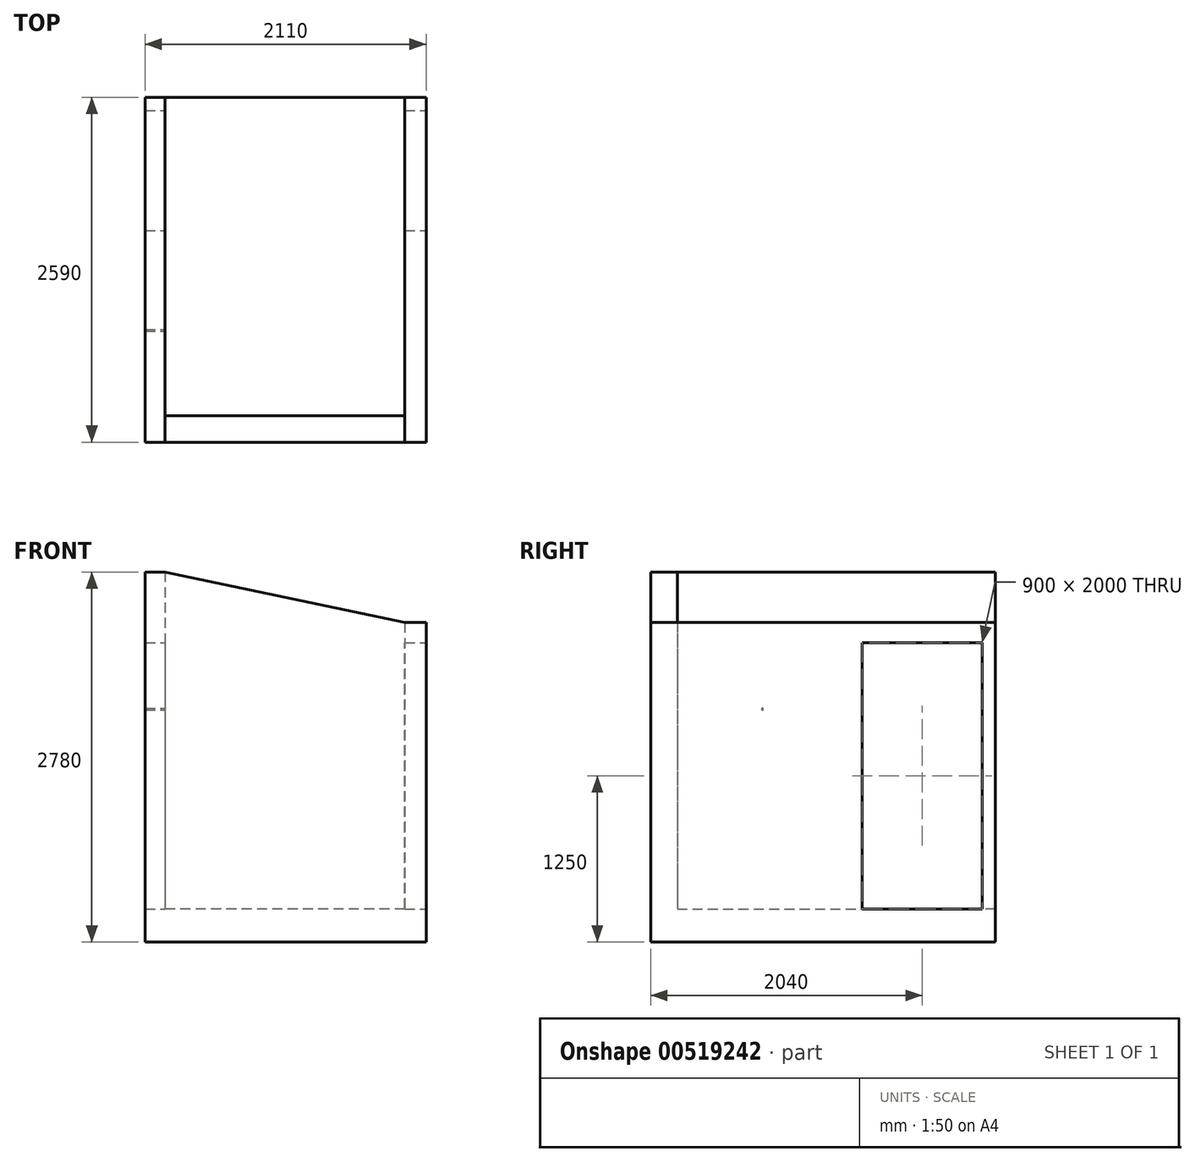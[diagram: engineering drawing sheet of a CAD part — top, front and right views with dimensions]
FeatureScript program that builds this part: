
annotation { "Feature Type Name" : "Feature", "Feature Type Description" : "" }
export const myFeature = defineFeature(function(context is Context, id is Id, definition is map)
    precondition{}
    {
        {
            var Q0;
            Q0=qCreatedBy(makeId("Top.planeOp"),FACE);
            var sketch = newSketch(context, id + "F0", { "sketchPlane" : qUnion([Q0])});
            skLineSegment(sketch, "E0.bottom", {"start": v(0, 0) * mm, "end": v(10600, 0) * mm});
            skLineSegment(sketch, "E0.top", {"start": v(0, -6350) * mm, "end": v(9400, -6350) * mm});
            skLineSegment(sketch, "E0.left", {"start": v(0, 0) * mm, "end": v(0, -6350) * mm});
            skLineSegment(sketch, "E0.right", {"start": v(10600, 0) * mm, "end": v(10600, -5300) * mm});
            skLineSegment(sketch, "E1.top", {"start": v(10600, -5300) * mm, "end": v(9400, -5300) * mm});
            skLineSegment(sketch, "E1.right", {"start": v(9400, -6350) * mm, "end": v(9400, -5300) * mm});
            skLineSegment(sketch, "E2.top", {"start": v(3900, -5150) * mm, "end": v(6300, -5150) * mm});
            skLineSegment(sketch, "E2.left", {"start": v(3900, -6150) * mm, "end": v(3900, -5150) * mm});
            skLineSegment(sketch, "E2.right", {"start": v(6300, -6150) * mm, "end": v(6300, -5150) * mm});
            skLineSegment(sketch, "E3.top", {"start": v(3900, -6150) * mm, "end": v(6300, -6150) * mm});
            skSolve(sketch);
        }
        {
            var Q0;
            Q0=qSketchRegion(id+"F0",true);
            extrude(context, id + "F1", {"entities" : qUnion([Q0]), "depth" : 250 * mm});
        }
        {
            var Q0;
            Q0=makeQuery(id+"F1.opExtrude","CAP_FACE",FACE,{"disambiguationData":[OSD([sQuery(id+"F0.wireOp",EDGE,"E0.bottom"),sQuery(id+"F0.wireOp",EDGE,"E0.top"),sQuery(id+"F0.wireOp",EDGE,"E0.left"),sQuery(id+"F0.wireOp",EDGE,"E0.right")])],"isStart":false});
            var sketch = newSketch(context, id + "F2", { "sketchPlane" : qUnion([Q0])});
            skLineSegment(sketch, "E4.bottom", {"start": v(200, -200) * mm, "end": v(3750, -200) * mm});
            skLineSegment(sketch, "E4.top", {"start": v(200, -6150) * mm, "end": v(3750, -6150) * mm});
            skLineSegment(sketch, "E4.left", {"start": v(200, -200) * mm, "end": v(200, -6150) * mm});
            skLineSegment(sketch, "E4.right", {"start": v(10400, -300) * mm, "end": v(10400, -3610) * mm});
            skLineSegment(sketch, "E5.bottom", {"start": v(9240, -6150) * mm, "end": v(7440, -6150) * mm});
            skLineSegment(sketch, "E5.top", {"start": v(10400, -3610) * mm, "end": v(7440, -3610) * mm});
            skLineSegment(sketch, "E6.top", {"start": v(3750, -5050) * mm, "end": v(3900, -5050) * mm});
            skLineSegment(sketch, "E6.left", {"start": v(3750, -6150) * mm, "end": v(3750, -5050) * mm});
            skLineSegment(sketch, "E6.right", {"start": v(3900, -6150) * mm, "end": v(3900, -5050) * mm});
            skLineSegment(sketch, "E7.top", {"start": v(3750, -300) * mm, "end": v(3900, -300) * mm});
            skLineSegment(sketch, "E7.left", {"start": v(3750, -200) * mm, "end": v(3750, -300) * mm});
            skLineSegment(sketch, "E7.right", {"start": v(3900, -280) * mm, "end": v(3900, -300) * mm});
            skLineSegment(sketch, "E8.top", {"start": v(4800, -1180) * mm, "end": v(4950, -1180) * mm});
            skLineSegment(sketch, "E8.left", {"start": v(4800, -280) * mm, "end": v(4800, -1180) * mm});
            skLineSegment(sketch, "E8.right", {"start": v(4950, -400) * mm, "end": v(4950, -1180) * mm});
            skLineSegment(sketch, "E9.top", {"start": v(7290, -300) * mm, "end": v(7440, -300) * mm});
            skLineSegment(sketch, "E9.left", {"start": v(7290, -200) * mm, "end": v(7290, -300) * mm});
            skLineSegment(sketch, "E10.top", {"start": v(9240, -3760) * mm, "end": v(7440, -3760) * mm});
            skLineSegment(sketch, "E10.right", {"start": v(7440, -6150) * mm, "end": v(7440, -3760) * mm});
            skLineSegment(sketch, "E11.top", {"start": v(7290, -2960) * mm, "end": v(7440, -2960) * mm});
            skLineSegment(sketch, "E11.left", {"start": v(7290, -6150) * mm, "end": v(7290, -2960) * mm});
            skLineSegment(sketch, "E11.right", {"start": v(7440, -3610) * mm, "end": v(7440, -2960) * mm});
            skLineSegment(sketch, "E12.bottom", {"start": v(0, 0) * mm, "end": v(10600, 0) * mm});
            skLineSegment(sketch, "E12.top", {"start": v(0, -6350) * mm, "end": v(9400, -6350) * mm});
            skLineSegment(sketch, "E12.left", {"start": v(0, 0) * mm, "end": v(0, -6350) * mm});
            skLineSegment(sketch, "E12.right", {"start": v(10600, 0) * mm, "end": v(10600, -3760) * mm});
            skLineSegment(sketch, "E13.trimOffspring", {"start": v(5250, -200) * mm, "end": v(7290, -200) * mm});
            skLineSegment(sketch, "E14.trimOffspring", {"start": v(3900, -6150) * mm, "end": v(7290, -6150) * mm});
            skLineSegment(sketch, "E15.top", {"start": v(4950, -400) * mm, "end": v(5250, -400) * mm});
            skLineSegment(sketch, "E15.right", {"start": v(5250, -200) * mm, "end": v(5250, -400) * mm});
            skLineSegment(sketch, "E16.top", {"start": v(3900, -280) * mm, "end": v(4800, -280) * mm});
            skLineSegment(sketch, "E17.trimOffspring", {"start": v(7440, -6150) * mm, "end": v(9240, -6150) * mm});
            skLineSegment(sketch, "E18.trimOffspring", {"start": v(9240, -3760) * mm, "end": v(9240, -6150) * mm});
            skLineSegment(sketch, "E19", {"start": v(10600, -3760) * mm, "end": v(9400, -3760) * mm});
            skLineSegment(sketch, "E20", {"start": v(9400, -3760) * mm, "end": v(9400, -6350) * mm});
            skLineSegment(sketch, "E21", {"start": v(7440, -300) * mm, "end": v(10400, -300) * mm});
            skSolve(sketch);
        }
        {
            var Q0;
            Q0=qSketchRegion(id+"F2",true);
            extrude(context, id + "F3", {"entities" : qUnion([Q0]), "operationType" : NewBodyOperationType.ADD, "depth" : 2320 * mm});
        }
        {
            var Q0;
            Q0=makeQuery(id+"F3.boolean.opBoolean","MERGE",FACE,{"derivedFrom":[makeQuery(id+"F1.opExtrude","SWEPT_FACE",FACE,{"disambiguationData":[OSD([sQuery(id+"F0.wireOp",EDGE,"E1.right")])]}),makeQuery(id+"F3.opExtrude","SWEPT_FACE",FACE,{"disambiguationData":[OSD([sQuery(id+"F2.wireOp",EDGE,"E20")])]})]});
            var sketch = newSketch(context, id + "F4", { "sketchPlane" : qUnion([Q0])});
            skLineSegment(sketch, "E22.bottom", {"start": v(-4760, 250) * mm, "end": v(-3860, 250) * mm});
            skLineSegment(sketch, "E22.top", {"start": v(-4760, 2250) * mm, "end": v(-3860, 2250) * mm});
            skLineSegment(sketch, "E22.left", {"start": v(-4760, 250) * mm, "end": v(-4760, 2250) * mm});
            skLineSegment(sketch, "E22.right", {"start": v(-3860, 250) * mm, "end": v(-3860, 2250) * mm});
            skSolve(sketch);
        }
        {
            var Q0;
            Q0=qSketchRegion(id+"F4",true);
            extrude(context, id + "F5", {"entities" : qUnion([Q0]), "operationType" : NewBodyOperationType.REMOVE, "endBound" : BoundingType.THROUGH_ALL, "oppositeDirection" : true, "depth" : 3000 * mm});
        }
        {
            var Q0;
            Q0=makeQuery(id+"F3.boolean.opBoolean","MERGE",FACE,{"derivedFrom":[makeQuery(id+"F1.opExtrude","SWEPT_FACE",FACE,{"disambiguationData":[OSD([sQuery(id+"F0.wireOp",EDGE,"E0.top")])]}),makeQuery(id+"F3.opExtrude","SWEPT_FACE",FACE,{"disambiguationData":[OSD([sQuery(id+"F2.wireOp",EDGE,"E12.top")])]})]});
            var sketch = newSketch(context, id + "F6", { "sketchPlane" : qUnion([Q0])});
            skLineSegment(sketch, "E23.bottom", {"start": v(7240, 2200) * mm, "end": v(6240, 2200) * mm});
            skLineSegment(sketch, "E23.top", {"start": v(7240, 800) * mm, "end": v(6240, 800) * mm});
            skLineSegment(sketch, "E23.left", {"start": v(7240, 2200) * mm, "end": v(7240, 800) * mm});
            skLineSegment(sketch, "E23.right", {"start": v(6240, 2200) * mm, "end": v(6240, 800) * mm});
            skLineSegment(sketch, "E24.bottom", {"start": v(2600, 2200) * mm, "end": v(3600, 2200) * mm});
            skLineSegment(sketch, "E24.top", {"start": v(2600, 800) * mm, "end": v(3600, 800) * mm});
            skLineSegment(sketch, "E24.left", {"start": v(2600, 2200) * mm, "end": v(2600, 800) * mm});
            skLineSegment(sketch, "E24.right", {"start": v(3600, 2200) * mm, "end": v(3600, 800) * mm});
            skLineSegment(sketch, "E25.bottom", {"start": v(9450, 2200) * mm, "end": v(10350, 2200) * mm});
            skLineSegment(sketch, "E25.top", {"start": v(9450, 1800) * mm, "end": v(10350, 1800) * mm});
            skLineSegment(sketch, "E25.left", {"start": v(9450, 2200) * mm, "end": v(9450, 1800) * mm});
            skLineSegment(sketch, "E25.right", {"start": v(10350, 2200) * mm, "end": v(10350, 1800) * mm});
            skSolve(sketch);
        }
        {
            var Q0;
            Q0=qSketchRegion(id+"F6",true);
            var Q1;
            Q1=makeQuery(id+"F3.opExtrude","SWEPT_FACE",FACE,{"disambiguationData":[OSD([sQuery(id+"F2.wireOp",EDGE,"E9.top"),sQuery(id+"F2.wireOp",EDGE,"E21")])]});
            extrude(context, id + "F7", {"entities" : qUnion([Q0]), "operationType" : NewBodyOperationType.REMOVE, "endBound" : BoundingType.UP_TO_SURFACE, "oppositeDirection" : true, "endBoundEntityFace" : qUnion([Q1]), "depth" : 25 * mm});
        }
        {
            var Q0;
            Q0=makeQuery(id+"F3.opExtrude","SWEPT_FACE",FACE,{"disambiguationData":[OSD([sQuery(id+"F2.wireOp",EDGE,"E4.right")])]});
            var sketch = newSketch(context, id + "F8", { "sketchPlane" : qUnion([Q0])});
            skLineSegment(sketch, "E26.bottom", {"start": v(680, 2100) * mm, "end": v(1600, 2100) * mm});
            skLineSegment(sketch, "E26.top", {"start": v(680, 1180) * mm, "end": v(1600, 1180) * mm});
            skLineSegment(sketch, "E26.left", {"start": v(680, 2100) * mm, "end": v(680, 1180) * mm});
            skLineSegment(sketch, "E26.right", {"start": v(1600, 2100) * mm, "end": v(1600, 1180) * mm});
            skLineSegment(sketch, "E27.bottom", {"start": v(1860, 2100) * mm, "end": v(2860, 2100) * mm});
            skLineSegment(sketch, "E27.top", {"start": v(1860, 1180) * mm, "end": v(2860, 1180) * mm});
            skLineSegment(sketch, "E27.left", {"start": v(1860, 2100) * mm, "end": v(1860, 1180) * mm});
            skLineSegment(sketch, "E27.right", {"start": v(2860, 2100) * mm, "end": v(2860, 1180) * mm});
            skSolve(sketch);
        }
        {
            var Q0;
            Q0=qSketchRegion(id+"F8",true);
            extrude(context, id + "F9", {"entities" : qUnion([Q0]), "operationType" : NewBodyOperationType.REMOVE, "endBound" : BoundingType.UP_TO_NEXT, "oppositeDirection" : true, "depth" : 25 * mm});
        }
        {
            var Q0;
            Q0=makeQuery(id+"F3.opExtrude","SWEPT_FACE",FACE,{"disambiguationData":[OSD([sQuery(id+"F2.wireOp",EDGE,"E4.left")])]});
            var sketch = newSketch(context, id + "F10", { "sketchPlane" : qUnion([Q0])});
            skLineSegment(sketch, "E28.bottom", {"start": v(-3660, 2250) * mm, "end": v(-2660, 2250) * mm});
            skLineSegment(sketch, "E28.top", {"start": v(-3660, 750) * mm, "end": v(-2660, 750) * mm});
            skLineSegment(sketch, "E28.left", {"start": v(-3660, 2250) * mm, "end": v(-3660, 750) * mm});
            skLineSegment(sketch, "E28.right", {"start": v(-2660, 2250) * mm, "end": v(-2660, 750) * mm});
            skLineSegment(sketch, "E29.bottom", {"start": v(-2560, 2250) * mm, "end": v(-1560, 2250) * mm});
            skLineSegment(sketch, "E29.top", {"start": v(-2560, 750) * mm, "end": v(-1560, 750) * mm});
            skLineSegment(sketch, "E29.left", {"start": v(-2560, 2250) * mm, "end": v(-2560, 750) * mm});
            skLineSegment(sketch, "E29.right", {"start": v(-1560, 2250) * mm, "end": v(-1560, 750) * mm});
            skLineSegment(sketch, "E30.bottom", {"start": v(-1460, 2250) * mm, "end": v(-460, 2250) * mm});
            skLineSegment(sketch, "E30.top", {"start": v(-1460, 750) * mm, "end": v(-460, 750) * mm});
            skLineSegment(sketch, "E30.left", {"start": v(-1460, 2250) * mm, "end": v(-1460, 750) * mm});
            skLineSegment(sketch, "E30.right", {"start": v(-460, 2250) * mm, "end": v(-460, 750) * mm});
            skSolve(sketch);
        }
        {
            var Q0;
            Q0=qSketchRegion(id+"F10",true);
            extrude(context, id + "F11", {"entities" : qUnion([Q0]), "operationType" : NewBodyOperationType.REMOVE, "endBound" : BoundingType.UP_TO_NEXT, "oppositeDirection" : true, "depth" : 25 * mm});
        }
        {
            var Q0;
            Q0=makeQuery(id+"F3.opExtrude","CAP_FACE",FACE,{"disambiguationData":[OSD([sQuery(id+"F2.wireOp",EDGE,"E4.bottom"),sQuery(id+"F2.wireOp",EDGE,"E4.top"),sQuery(id+"F2.wireOp",EDGE,"E4.left"),sQuery(id+"F2.wireOp",EDGE,"E4.right"),sQuery(id+"F2.wireOp",EDGE,"E5.top"),sQuery(id+"F2.wireOp",EDGE,"E6.top"),sQuery(id+"F2.wireOp",EDGE,"E6.left"),sQuery(id+"F2.wireOp",EDGE,"E6.right"),sQuery(id+"F2.wireOp",EDGE,"E7.top"),sQuery(id+"F2.wireOp",EDGE,"E7.left"),sQuery(id+"F2.wireOp",EDGE,"E7.right"),sQuery(id+"F2.wireOp",EDGE,"E8.top"),sQuery(id+"F2.wireOp",EDGE,"E8.left"),sQuery(id+"F2.wireOp",EDGE,"E8.right"),sQuery(id+"F2.wireOp",EDGE,"E9.top"),sQuery(id+"F2.wireOp",EDGE,"E9.left"),sQuery(id+"F2.wireOp",EDGE,"E9.right"),sQuery(id+"F2.wireOp",EDGE,"E10.top"),sQuery(id+"F2.wireOp",EDGE,"E10.right"),sQuery(id+"F2.wireOp",EDGE,"E11.top"),sQuery(id+"F2.wireOp",EDGE,"E11.left"),sQuery(id+"F2.wireOp",EDGE,"E11.right"),sQuery(id+"F2.wireOp",EDGE,"E12.bottom"),sQuery(id+"F2.wireOp",EDGE,"E12.top"),sQuery(id+"F2.wireOp",EDGE,"E12.left"),sQuery(id+"F2.wireOp",EDGE,"E12.right"),sQuery(id+"F2.wireOp",EDGE,"E13.trimOffspring"),sQuery(id+"F2.wireOp",EDGE,"f96be5dc-ae23-419c-a534-e8c19ccc8482.trimOffspring"),sQuery(id+"F2.wireOp",EDGE,"E14.trimOffspring"),sQuery(id+"F2.wireOp",EDGE,"E15.top"),sQuery(id+"F2.wireOp",EDGE,"E15.right"),sQuery(id+"F2.wireOp",EDGE,"E16.top"),sQuery(id+"F2.wireOp",EDGE,"E17.trimOffspring"),sQuery(id+"F2.wireOp",EDGE,"E18.trimOffspring"),sQuery(id+"F2.wireOp",EDGE,"E19"),sQuery(id+"F2.wireOp",EDGE,"E20")])],"isStart":false});
            var sketch = newSketch(context, id + "F12", { "sketchPlane" : qUnion([Q0])});
            skLineSegment(sketch, "E31.bottom", {"start": v(7290, -300) * mm, "end": v(7440, -300) * mm});
            skLineSegment(sketch, "E31.top", {"start": v(7290, -2960) * mm, "end": v(7440, -2960) * mm});
            skLineSegment(sketch, "E31.left", {"start": v(7290, -300) * mm, "end": v(7290, -2960) * mm});
            skLineSegment(sketch, "E31.right", {"start": v(7440, -300) * mm, "end": v(7440, -2960) * mm});
            skSolve(sketch);
        }
        {
            var Q0;
            Q0=qSketchRegion(id+"F12",true);
            extrude(context, id + "F13", {"entities" : qUnion([Q0]), "operationType" : NewBodyOperationType.ADD, "oppositeDirection" : true, "depth" : 280 * mm});
        }
        {
            var Q0;
            Q0=makeQuery(id+"F3.boolean.opBoolean","MERGE",FACE,{"derivedFrom":[makeQuery(id+"F1.opExtrude","SWEPT_FACE",FACE,{"disambiguationData":[OSD([sQuery(id+"F0.wireOp",EDGE,"E3.top")])]}),makeQuery(id+"F3.opExtrude","SWEPT_FACE",FACE,{"disambiguationData":[OSD([sQuery(id+"F2.wireOp",EDGE,"E14.trimOffspring")])]})]});
            var sketch = newSketch(context, id + "F14", { "sketchPlane" : qUnion([Q0])});
            skLineSegment(sketch, "E32", {"start": v(-6350, 250) * mm, "end": v(-6350, 540) * mm});
            skLineSegment(sketch, "E33", {"start": v(-6350, 540) * mm, "end": v(-6045, 540) * mm});
            skLineSegment(sketch, "E34", {"start": v(-6045, 540) * mm, "end": v(-6045, 830) * mm});
            skLineSegment(sketch, "E35", {"start": v(-6045, 830) * mm, "end": v(-5740, 830) * mm});
            skLineSegment(sketch, "E36", {"start": v(-5740, 830) * mm, "end": v(-5740, 1120) * mm});
            skLineSegment(sketch, "E37", {"start": v(-5740, 1120) * mm, "end": v(-5435, 1120) * mm});
            skLineSegment(sketch, "E38", {"start": v(-5435, 1120) * mm, "end": v(-5435, 1410) * mm});
            skLineSegment(sketch, "E39", {"start": v(-5435, 1410) * mm, "end": v(-5130, 1410) * mm});
            skLineSegment(sketch, "E40", {"start": v(-5130, 1410) * mm, "end": v(-5130, 1700) * mm});
            skLineSegment(sketch, "E41", {"start": v(-5130, 1700) * mm, "end": v(-4825, 1700) * mm});
            skLineSegment(sketch, "E42", {"start": v(-4825, 1700) * mm, "end": v(-4825, 1990) * mm});
            skLineSegment(sketch, "E43", {"start": v(-4825, 1990) * mm, "end": v(-4520, 1990) * mm});
            skLineSegment(sketch, "E44", {"start": v(-4520, 1990) * mm, "end": v(-4520, 2280) * mm});
            skLineSegment(sketch, "E45", {"start": v(-4520, 2280) * mm, "end": v(-4215, 2280) * mm});
            skLineSegment(sketch, "E46", {"start": v(-4215, 2280) * mm, "end": v(-4215, 2570) * mm});
            skLineSegment(sketch, "E47", {"start": v(-4215, 2570) * mm, "end": v(-3900, 2570) * mm});
            skLineSegment(sketch, "E48.0", {"start": v(-4165, 2520) * mm, "end": v(-3900, 2520) * mm});
            skLineSegment(sketch, "E48.1", {"start": v(-4165, 2230) * mm, "end": v(-4165, 2520) * mm});
            skLineSegment(sketch, "E48.2", {"start": v(-4470, 2230) * mm, "end": v(-4165, 2230) * mm});
            skLineSegment(sketch, "E48.3", {"start": v(-4470, 1940) * mm, "end": v(-4470, 2230) * mm});
            skLineSegment(sketch, "E48.4", {"start": v(-4775, 1940) * mm, "end": v(-4470, 1940) * mm});
            skLineSegment(sketch, "E48.5", {"start": v(-4775, 1650) * mm, "end": v(-4775, 1940) * mm});
            skLineSegment(sketch, "E48.6", {"start": v(-5995, 780) * mm, "end": v(-5690, 780) * mm});
            skLineSegment(sketch, "E48.7", {"start": v(-5995, 490) * mm, "end": v(-5995, 780) * mm});
            skLineSegment(sketch, "E48.8", {"start": v(-6300, 490) * mm, "end": v(-5995, 490) * mm});
            skLineSegment(sketch, "E48.9", {"start": v(-6300, 250) * mm, "end": v(-6300, 490) * mm});
            skLineSegment(sketch, "E48.10", {"start": v(-5690, 780) * mm, "end": v(-5690, 1070) * mm});
            skLineSegment(sketch, "E48.11", {"start": v(-5690, 1070) * mm, "end": v(-5385, 1070) * mm});
            skLineSegment(sketch, "E48.12", {"start": v(-5385, 1070) * mm, "end": v(-5385, 1360) * mm});
            skLineSegment(sketch, "E48.13", {"start": v(-5385, 1360) * mm, "end": v(-5080, 1360) * mm});
            skLineSegment(sketch, "E48.14", {"start": v(-5080, 1360) * mm, "end": v(-5080, 1650) * mm});
            skLineSegment(sketch, "E48.15", {"start": v(-5080, 1650) * mm, "end": v(-4775, 1650) * mm});
            skLineSegment(sketch, "E49", {"start": v(-3900, 2570) * mm, "end": v(-3900, 2520) * mm});
            skLineSegment(sketch, "E50", {"start": v(-6350, 250) * mm, "end": v(-6300, 250) * mm});
            skLineSegment(sketch, "E51", {"start": v(-3900, 2570) * mm, "end": v(-3900, 250) * mm, "construction": true});
            skSolve(sketch);
        }
        {
            var Q0;
            Q0=qSketchRegion(id+"F14",true);
            extrude(context, id + "F15", {"entities" : qUnion([Q0]), "operationType" : NewBodyOperationType.ADD, "depth" : 950 * mm});
        }
        {
            var Q0;
            Q0=makeQuery(id+"F15.opExtrude","CAP_FACE",FACE,{"disambiguationData":[OSD([sQuery(id+"F14.wireOp",EDGE,"E32"),sQuery(id+"F14.wireOp",EDGE,"E33"),sQuery(id+"F14.wireOp",EDGE,"E34"),sQuery(id+"F14.wireOp",EDGE,"E35"),sQuery(id+"F14.wireOp",EDGE,"E36"),sQuery(id+"F14.wireOp",EDGE,"E37"),sQuery(id+"F14.wireOp",EDGE,"E38"),sQuery(id+"F14.wireOp",EDGE,"E39"),sQuery(id+"F14.wireOp",EDGE,"E40"),sQuery(id+"F14.wireOp",EDGE,"E41"),sQuery(id+"F14.wireOp",EDGE,"E42"),sQuery(id+"F14.wireOp",EDGE,"E43"),sQuery(id+"F14.wireOp",EDGE,"E44"),sQuery(id+"F14.wireOp",EDGE,"E45"),sQuery(id+"F14.wireOp",EDGE,"E46"),sQuery(id+"F14.wireOp",EDGE,"E47"),sQuery(id+"F14.wireOp",EDGE,"E48.0"),sQuery(id+"F14.wireOp",EDGE,"E48.1"),sQuery(id+"F14.wireOp",EDGE,"E48.2"),sQuery(id+"F14.wireOp",EDGE,"E48.3"),sQuery(id+"F14.wireOp",EDGE,"E48.4"),sQuery(id+"F14.wireOp",EDGE,"E48.5"),sQuery(id+"F14.wireOp",EDGE,"E48.6"),sQuery(id+"F14.wireOp",EDGE,"E48.7"),sQuery(id+"F14.wireOp",EDGE,"E48.8"),sQuery(id+"F14.wireOp",EDGE,"E48.9"),sQuery(id+"F14.wireOp",EDGE,"E48.10"),sQuery(id+"F14.wireOp",EDGE,"E48.11"),sQuery(id+"F14.wireOp",EDGE,"E48.12"),sQuery(id+"F14.wireOp",EDGE,"E48.13"),sQuery(id+"F14.wireOp",EDGE,"E48.14"),sQuery(id+"F14.wireOp",EDGE,"E48.15"),sQuery(id+"F14.wireOp",EDGE,"E49"),sQuery(id+"F14.wireOp",EDGE,"E50")])],"isStart":false});
            var sketch = newSketch(context, id + "F16", { "sketchPlane" : qUnion([Q0])});
            skLineSegment(sketch, "E52", {"start": v(-6350, 540) * mm, "end": v(-4215, 2570) * mm});
            skLineSegment(sketch, "E53", {"start": v(-3900, 2570) * mm, "end": v(-3900, 2475.76) * mm});
            skLineSegment(sketch, "E54", {"start": v(-6300, 250) * mm, "end": v(-4165, 2230) * mm});
            skLineSegment(sketch, "E55", {"start": v(-4165, 2230) * mm, "end": v(-3900, 2475.76) * mm});
            skLineSegment(sketch, "E56", {"start": v(-6350, 540) * mm, "end": v(-6350, 250) * mm});
            skLineSegment(sketch, "E57", {"start": v(-6350, 250) * mm, "end": v(-6300, 250) * mm});
            skLineSegment(sketch, "E58", {"start": v(-4215, 2570) * mm, "end": v(-3900, 2570) * mm});
            skSolve(sketch);
        }
        {
            var Q0;
            Q0=qSketchRegion(id+"F16",true);
            extrude(context, id + "F17", {"entities" : qUnion([Q0]), "operationType" : NewBodyOperationType.ADD, "depth" : 50 * mm});
        }
        {
            var Q0;
            {var subQ0=sQuery(id+"F0.wireOp",EDGE,"E3.top");var subQ1=sQuery(id+"F0.wireOp",EDGE,"E2.right");var subQ2=sQuery(id+"F0.wireOp",EDGE,"E2.left");var subQ3=sQuery(id+"F0.wireOp",EDGE,"E2.top");var subQ4=sQuery(id+"F0.wireOp",EDGE,"E1.right");var subQ5=sQuery(id+"F0.wireOp",EDGE,"E1.top");var subQ6=sQuery(id+"F0.wireOp",EDGE,"E0.right");var subQ7=makeQuery(id+"F1.opExtrude","CAP_FACE",FACE,{"disambiguationData":[OSD([sQuery(id+"F0.wireOp",EDGE,"E0.bottom"),sQuery(id+"F0.wireOp",EDGE,"E0.top"),sQuery(id+"F0.wireOp",EDGE,"E0.left"),subQ6,subQ5,subQ4,subQ3,subQ2,subQ1,subQ0])],"isStart":false});Q0=makeQuery(id+"F5.boolean.opBoolean","MERGE",FACE,{"derivedFrom":[makeQuery(id+"F3.boolean.opBoolean","SPLIT",FACE,{"disambiguationData":[TD([makeQuery(id+"F1.opExtrude","SWEPT_FACE",FACE,{"disambiguationData":[OSD([subQ6])]})])],"derivedFrom":subQ7}),makeQuery(id+"F3.boolean.opBoolean","SPLIT",FACE,{"disambiguationData":[TD([makeQuery(id+"F1.opExtrude","SWEPT_FACE",FACE,{"disambiguationData":[OSD([subQ3])]})])],"derivedFrom":subQ7}),makeQuery(id+"F3.boolean.opBoolean","SPLIT",FACE,{"disambiguationData":[TD([makeQuery(id+"F3.opExtrude","SWEPT_FACE",FACE,{"disambiguationData":[OSD([sQuery(id+"F2.wireOp",EDGE,"E10.top")])]})])],"derivedFrom":subQ7}),makeQuery(id+"F5.opExtrude","SWEPT_FACE",FACE,{"disambiguationData":[OSD([sQuery(id+"F4.wireOp",EDGE,"E22.bottom")])]})]});}
            var sketch = newSketch(context, id + "F18", { "sketchPlane" : qUnion([Q0])});
            skLineSegment(sketch, "E59.bottom", {"start": v(6045, -5150) * mm, "end": v(6005, -5150) * mm});
            skLineSegment(sketch, "E59.top", {"start": v(6045, -5100) * mm, "end": v(6005, -5100) * mm});
            skLineSegment(sketch, "E59.left", {"start": v(6050, -5145) * mm, "end": v(6050, -5105) * mm});
            skLineSegment(sketch, "E59.right", {"start": v(6000, -5145) * mm, "end": v(6000, -5105) * mm});
            skPoint(sketch, "E60.visualSharp", {"position": v(6000, -5100) * mm});
            skArc(sketch, "E60.filletArc", {"start": v(6005, -5100) * mm, "mid": v(6001.46, -5101.46) * mm, "end": v(6000, -5105) * mm});
            skPoint(sketch, "E61.visualSharp", {"position": v(6050, -5100) * mm});
            skArc(sketch, "E61.filletArc", {"start": v(6050, -5105) * mm, "mid": v(6048.54, -5101.46) * mm, "end": v(6045, -5100) * mm});
            skPoint(sketch, "E62.visualSharp", {"position": v(6050, -5150) * mm});
            skArc(sketch, "E62.filletArc", {"start": v(6045, -5150) * mm, "mid": v(6048.54, -5148.54) * mm, "end": v(6050, -5145) * mm});
            skPoint(sketch, "E63.visualSharp", {"position": v(6000, -5150) * mm});
            skArc(sketch, "E63.filletArc", {"start": v(6000, -5145) * mm, "mid": v(6001.46, -5148.54) * mm, "end": v(6005, -5150) * mm});
            skPoint(sketch, "E64.1.0.0", {"position": v(5700, -5150) * mm});
            skLineSegment(sketch, "E64.1.0.1", {"start": v(5745, -5150) * mm, "end": v(5705, -5150) * mm});
            skLineSegment(sketch, "E64.1.0.2", {"start": v(5745, -5100) * mm, "end": v(5705, -5100) * mm});
            skPoint(sketch, "E64.1.0.3", {"position": v(5700, -5100) * mm});
            skLineSegment(sketch, "E64.1.0.4", {"start": v(5750, -5145) * mm, "end": v(5750, -5105) * mm});
            skPoint(sketch, "E64.1.0.5", {"position": v(5750, -5100) * mm});
            skPoint(sketch, "E64.1.0.6", {"position": v(5750, -5150) * mm});
            skLineSegment(sketch, "E64.1.0.7", {"start": v(5700, -5145) * mm, "end": v(5700, -5105) * mm});
            skArc(sketch, "E64.1.0.8", {"start": v(5750, -5105) * mm, "mid": v(5748.54, -5101.46) * mm, "end": v(5745, -5100) * mm});
            skArc(sketch, "E64.1.0.9", {"start": v(5705, -5100) * mm, "mid": v(5701.46, -5101.46) * mm, "end": v(5700, -5105) * mm});
            skArc(sketch, "E64.1.0.10", {"start": v(5700, -5145) * mm, "mid": v(5701.46, -5148.54) * mm, "end": v(5705, -5150) * mm});
            skArc(sketch, "E64.1.0.11", {"start": v(5745, -5150) * mm, "mid": v(5748.54, -5148.54) * mm, "end": v(5750, -5145) * mm});
            skPoint(sketch, "E64.2.0.0", {"position": v(5400, -5150) * mm});
            skLineSegment(sketch, "E64.2.0.1", {"start": v(5445, -5150) * mm, "end": v(5405, -5150) * mm});
            skLineSegment(sketch, "E64.2.0.2", {"start": v(5445, -5100) * mm, "end": v(5405, -5100) * mm});
            skPoint(sketch, "E64.2.0.3", {"position": v(5400, -5100) * mm});
            skLineSegment(sketch, "E64.2.0.4", {"start": v(5450, -5145) * mm, "end": v(5450, -5105) * mm});
            skPoint(sketch, "E64.2.0.5", {"position": v(5450, -5100) * mm});
            skPoint(sketch, "E64.2.0.6", {"position": v(5450, -5150) * mm});
            skLineSegment(sketch, "E64.2.0.7", {"start": v(5400, -5145) * mm, "end": v(5400, -5105) * mm});
            skArc(sketch, "E64.2.0.8", {"start": v(5450, -5105) * mm, "mid": v(5448.54, -5101.46) * mm, "end": v(5445, -5100) * mm});
            skArc(sketch, "E64.2.0.9", {"start": v(5405, -5100) * mm, "mid": v(5401.46, -5101.46) * mm, "end": v(5400, -5105) * mm});
            skArc(sketch, "E64.2.0.10", {"start": v(5400, -5145) * mm, "mid": v(5401.46, -5148.54) * mm, "end": v(5405, -5150) * mm});
            skArc(sketch, "E64.2.0.11", {"start": v(5445, -5150) * mm, "mid": v(5448.54, -5148.54) * mm, "end": v(5450, -5145) * mm});
            skPoint(sketch, "E64.3.0.0", {"position": v(5100, -5150) * mm});
            skLineSegment(sketch, "E64.3.0.1", {"start": v(5145, -5150) * mm, "end": v(5105, -5150) * mm});
            skLineSegment(sketch, "E64.3.0.2", {"start": v(5145, -5100) * mm, "end": v(5105, -5100) * mm});
            skPoint(sketch, "E64.3.0.3", {"position": v(5100, -5100) * mm});
            skLineSegment(sketch, "E64.3.0.4", {"start": v(5150, -5145) * mm, "end": v(5150, -5105) * mm});
            skPoint(sketch, "E64.3.0.5", {"position": v(5150, -5100) * mm});
            skPoint(sketch, "E64.3.0.6", {"position": v(5150, -5150) * mm});
            skLineSegment(sketch, "E64.3.0.7", {"start": v(5100, -5145) * mm, "end": v(5100, -5105) * mm});
            skArc(sketch, "E64.3.0.8", {"start": v(5150, -5105) * mm, "mid": v(5148.54, -5101.46) * mm, "end": v(5145, -5100) * mm});
            skArc(sketch, "E64.3.0.9", {"start": v(5105, -5100) * mm, "mid": v(5101.46, -5101.46) * mm, "end": v(5100, -5105) * mm});
            skArc(sketch, "E64.3.0.10", {"start": v(5100, -5145) * mm, "mid": v(5101.46, -5148.54) * mm, "end": v(5105, -5150) * mm});
            skArc(sketch, "E64.3.0.11", {"start": v(5145, -5150) * mm, "mid": v(5148.54, -5148.54) * mm, "end": v(5150, -5145) * mm});
            skPoint(sketch, "E64.4.0.0", {"position": v(4800, -5150) * mm});
            skLineSegment(sketch, "E64.4.0.1", {"start": v(4845, -5150) * mm, "end": v(4805, -5150) * mm});
            skLineSegment(sketch, "E64.4.0.2", {"start": v(4845, -5100) * mm, "end": v(4805, -5100) * mm});
            skPoint(sketch, "E64.4.0.3", {"position": v(4800, -5100) * mm});
            skLineSegment(sketch, "E64.4.0.4", {"start": v(4850, -5145) * mm, "end": v(4850, -5105) * mm});
            skPoint(sketch, "E64.4.0.5", {"position": v(4850, -5100) * mm});
            skPoint(sketch, "E64.4.0.6", {"position": v(4850, -5150) * mm});
            skLineSegment(sketch, "E64.4.0.7", {"start": v(4800, -5145) * mm, "end": v(4800, -5105) * mm});
            skArc(sketch, "E64.4.0.8", {"start": v(4850, -5105) * mm, "mid": v(4848.54, -5101.46) * mm, "end": v(4845, -5100) * mm});
            skArc(sketch, "E64.4.0.9", {"start": v(4805, -5100) * mm, "mid": v(4801.46, -5101.46) * mm, "end": v(4800, -5105) * mm});
            skArc(sketch, "E64.4.0.10", {"start": v(4800, -5145) * mm, "mid": v(4801.46, -5148.54) * mm, "end": v(4805, -5150) * mm});
            skArc(sketch, "E64.4.0.11", {"start": v(4845, -5150) * mm, "mid": v(4848.54, -5148.54) * mm, "end": v(4850, -5145) * mm});
            skPoint(sketch, "E64.5.0.0", {"position": v(4500, -5150) * mm});
            skLineSegment(sketch, "E64.5.0.1", {"start": v(4545, -5150) * mm, "end": v(4505, -5150) * mm});
            skLineSegment(sketch, "E64.5.0.2", {"start": v(4545, -5100) * mm, "end": v(4505, -5100) * mm});
            skPoint(sketch, "E64.5.0.3", {"position": v(4500, -5100) * mm});
            skLineSegment(sketch, "E64.5.0.4", {"start": v(4550, -5145) * mm, "end": v(4550, -5105) * mm});
            skPoint(sketch, "E64.5.0.5", {"position": v(4550, -5100) * mm});
            skPoint(sketch, "E64.5.0.6", {"position": v(4550, -5150) * mm});
            skLineSegment(sketch, "E64.5.0.7", {"start": v(4500, -5145) * mm, "end": v(4500, -5105) * mm});
            skArc(sketch, "E64.5.0.8", {"start": v(4550, -5105) * mm, "mid": v(4548.54, -5101.46) * mm, "end": v(4545, -5100) * mm});
            skArc(sketch, "E64.5.0.9", {"start": v(4505, -5100) * mm, "mid": v(4501.46, -5101.46) * mm, "end": v(4500, -5105) * mm});
            skArc(sketch, "E64.5.0.10", {"start": v(4500, -5145) * mm, "mid": v(4501.46, -5148.54) * mm, "end": v(4505, -5150) * mm});
            skArc(sketch, "E64.5.0.11", {"start": v(4545, -5150) * mm, "mid": v(4548.54, -5148.54) * mm, "end": v(4550, -5145) * mm});
            skLineSegment(sketch, "E64.direction1", {"start": v(6000, -5150) * mm, "end": v(5700, -5150) * mm, "construction": true});
            skSolve(sketch);
        }
        {
            var Q0;
            Q0=qSketchRegion(id+"F18",true);
            extrude(context, id + "F19", {"entities" : qUnion([Q0]), "operationType" : NewBodyOperationType.ADD, "depth" : 2320 * mm});
        }
        {
            var Q0;
            Q0=makeQuery(id+"F3.opExtrude","SWEPT_FACE",FACE,{"disambiguationData":[OSD([sQuery(id+"F2.wireOp",EDGE,"E19")])]});
            var sketch = newSketch(context, id + "F20", { "sketchPlane" : qUnion([Q0])});
            skLineSegment(sketch, "E65", {"start": v(9400, 2570) * mm, "end": v(10400, 2350) * mm});
            skLineSegment(sketch, "E66", {"start": v(10400, 2350) * mm, "end": v(10600, 2350) * mm});
            skLineSegment(sketch, "E67", {"start": v(10600, 2350) * mm, "end": v(10600, 2570) * mm});
            skLineSegment(sketch, "E68", {"start": v(10600, 2570) * mm, "end": v(9400, 2570) * mm});
            skSolve(sketch);
        }
        {
            var Q0;
            Q0=qSketchRegion(id+"F20",true);
            extrude(context, id + "F21", {"entities" : qUnion([Q0]), "operationType" : NewBodyOperationType.REMOVE, "endBound" : BoundingType.THROUGH_ALL, "oppositeDirection" : true, "depth" : 25 * mm});
        }
        {
            var Q0;
            {var subQ0=sQuery(id+"F0.wireOp",EDGE,"E3.top");var subQ1=sQuery(id+"F0.wireOp",EDGE,"E2.right");var subQ2=sQuery(id+"F0.wireOp",EDGE,"E2.left");var subQ3=sQuery(id+"F0.wireOp",EDGE,"E2.top");var subQ4=sQuery(id+"F0.wireOp",EDGE,"E1.right");var subQ5=sQuery(id+"F0.wireOp",EDGE,"E1.top");var subQ6=sQuery(id+"F0.wireOp",EDGE,"E0.right");var subQ7=makeQuery(id+"F1.opExtrude","CAP_FACE",FACE,{"disambiguationData":[OSD([sQuery(id+"F0.wireOp",EDGE,"E0.bottom"),sQuery(id+"F0.wireOp",EDGE,"E0.top"),sQuery(id+"F0.wireOp",EDGE,"E0.left"),subQ6,subQ5,subQ4,subQ3,subQ2,subQ1,subQ0])],"isStart":false});Q0=makeQuery(id+"F5.boolean.opBoolean","MERGE",FACE,{"derivedFrom":[makeQuery(id+"F3.boolean.opBoolean","SPLIT",FACE,{"disambiguationData":[TD([makeQuery(id+"F1.opExtrude","SWEPT_FACE",FACE,{"disambiguationData":[OSD([subQ6])]})])],"derivedFrom":subQ7}),makeQuery(id+"F3.boolean.opBoolean","SPLIT",FACE,{"disambiguationData":[TD([makeQuery(id+"F1.opExtrude","SWEPT_FACE",FACE,{"disambiguationData":[OSD([subQ3])]})])],"derivedFrom":subQ7}),makeQuery(id+"F3.boolean.opBoolean","SPLIT",FACE,{"disambiguationData":[TD([makeQuery(id+"F3.opExtrude","SWEPT_FACE",FACE,{"disambiguationData":[OSD([sQuery(id+"F2.wireOp",EDGE,"E10.top")])]})])],"derivedFrom":subQ7}),makeQuery(id+"F5.opExtrude","SWEPT_FACE",FACE,{"disambiguationData":[OSD([sQuery(id+"F4.wireOp",EDGE,"E22.bottom")])]})]});}
            var sketch = newSketch(context, id + "F22", { "sketchPlane" : qUnion([Q0])});
            skCircle(sketch, "E69", {"center": v(10300, -2510) * mm, "radius": 30 * mm});
            skSolve(sketch);
        }
        {
            var Q0;
            Q0=qSketchRegion(id+"F22",true);
            extrude(context, id + "F23", {"entities" : qUnion([Q0]), "operationType" : NewBodyOperationType.REMOVE, "endBound" : BoundingType.THROUGH_ALL, "oppositeDirection" : true, "depth" : 25 * mm});
        }
        {
            var Q0;
            Q0=makeQuery(id+"F3.opExtrude","SWEPT_FACE",FACE,{"disambiguationData":[OSD([sQuery(id+"F2.wireOp",EDGE,"E4.right")])]});
            var sketch = newSketch(context, id + "F24", { "sketchPlane" : qUnion([Q0])});
            skLineSegment(sketch, "E70.0", {"start": v(630, 2150) * mm, "end": v(630, 1130) * mm});
            skLineSegment(sketch, "E70.1", {"start": v(630, 2150) * mm, "end": v(1650, 2150) * mm});
            skLineSegment(sketch, "E70.2", {"start": v(1650, 2150) * mm, "end": v(1650, 1130) * mm});
            skLineSegment(sketch, "E70.3", {"start": v(630, 1130) * mm, "end": v(1650, 1130) * mm});
            skLineSegment(sketch, "E71.0", {"start": v(1810, 2150) * mm, "end": v(1810, 1130) * mm});
            skLineSegment(sketch, "E71.1", {"start": v(1810, 2150) * mm, "end": v(2910, 2150) * mm});
            skLineSegment(sketch, "E71.2", {"start": v(2910, 2150) * mm, "end": v(2910, 1130) * mm});
            skLineSegment(sketch, "E71.3", {"start": v(1810, 1130) * mm, "end": v(2910, 1130) * mm});
            skSolve(sketch);
        }
        {
            var Q0;
            Q0=qSketchRegion(id+"F24",true);
            extrude(context, id + "F25", {"entities" : qUnion([Q0]), "operationType" : NewBodyOperationType.REMOVE, "oppositeDirection" : true, "depth" : 50 * mm});
        }
        {
            var Q0;
            Q0=makeQuery(id+"F17.boolean.opBoolean","MERGE",FACE,{"derivedFrom":[makeQuery(id+"F15.boolean.opBoolean","MERGE",FACE,{"derivedFrom":[makeQuery(id+"F13.boolean.opBoolean","MERGE",FACE,{"derivedFrom":[makeQuery(id+"F3.opExtrude","CAP_FACE",FACE,{"disambiguationData":[OSD([sQuery(id+"F2.wireOp",EDGE,"E4.bottom"),sQuery(id+"F2.wireOp",EDGE,"E4.top"),sQuery(id+"F2.wireOp",EDGE,"E4.left"),sQuery(id+"F2.wireOp",EDGE,"E4.right"),sQuery(id+"F2.wireOp",EDGE,"E5.top"),sQuery(id+"F2.wireOp",EDGE,"E6.top"),sQuery(id+"F2.wireOp",EDGE,"E6.left"),sQuery(id+"F2.wireOp",EDGE,"E6.right"),sQuery(id+"F2.wireOp",EDGE,"E7.top"),sQuery(id+"F2.wireOp",EDGE,"E7.left"),sQuery(id+"F2.wireOp",EDGE,"E7.right"),sQuery(id+"F2.wireOp",EDGE,"E8.top"),sQuery(id+"F2.wireOp",EDGE,"E8.left"),sQuery(id+"F2.wireOp",EDGE,"E8.right"),sQuery(id+"F2.wireOp",EDGE,"E9.top"),sQuery(id+"F2.wireOp",EDGE,"E9.left"),sQuery(id+"F2.wireOp",EDGE,"E10.top"),sQuery(id+"F2.wireOp",EDGE,"E10.right"),sQuery(id+"F2.wireOp",EDGE,"E11.top"),sQuery(id+"F2.wireOp",EDGE,"E11.left"),sQuery(id+"F2.wireOp",EDGE,"E11.right"),sQuery(id+"F2.wireOp",EDGE,"E12.bottom"),sQuery(id+"F2.wireOp",EDGE,"E12.top"),sQuery(id+"F2.wireOp",EDGE,"E12.left"),sQuery(id+"F2.wireOp",EDGE,"E12.right"),sQuery(id+"F2.wireOp",EDGE,"E13.trimOffspring"),sQuery(id+"F2.wireOp",EDGE,"E14.trimOffspring"),sQuery(id+"F2.wireOp",EDGE,"E15.top"),sQuery(id+"F2.wireOp",EDGE,"E15.right"),sQuery(id+"F2.wireOp",EDGE,"E16.top"),sQuery(id+"F2.wireOp",EDGE,"E17.trimOffspring"),sQuery(id+"F2.wireOp",EDGE,"E18.trimOffspring"),sQuery(id+"F2.wireOp",EDGE,"E19"),sQuery(id+"F2.wireOp",EDGE,"E20"),sQuery(id+"F2.wireOp",EDGE,"E21")])],"isStart":false}),makeQuery(id+"F13.opExtrude","CAP_FACE",FACE,{"disambiguationData":[OSD([sQuery(id+"F12.wireOp",EDGE,"E31.bottom"),sQuery(id+"F12.wireOp",EDGE,"E31.top"),sQuery(id+"F12.wireOp",EDGE,"E31.left"),sQuery(id+"F12.wireOp",EDGE,"E31.right")])],"isStart":true})]}),makeQuery(id+"F15.opExtrude","SWEPT_FACE",FACE,{"disambiguationData":[OSD([sQuery(id+"F14.wireOp",EDGE,"E47")])]})]}),makeQuery(id+"F17.opExtrude","SWEPT_FACE",FACE,{"disambiguationData":[OSD([sQuery(id+"F16.wireOp",EDGE,"E58")])]})]});
            var sketch = newSketch(context, id + "F26", { "sketchPlane" : qUnion([Q0])});
            skLineSegment(sketch, "E72.bottom", {"start": v(10725.6, 0) * mm, "end": v(0, 0) * mm});
            skLineSegment(sketch, "E72.left", {"start": v(10725.6, 0) * mm, "end": v(10725.6, -3401.57) * mm});
            skLineSegment(sketch, "E72.right", {"start": v(0, 0) * mm, "end": v(0, -6350) * mm});
            skLineSegment(sketch, "E73.right", {"start": v(6873.54, -6350) * mm, "end": v(6873.54, -3401.57) * mm});
            skLineSegment(sketch, "E74", {"start": v(6873.54, -3401.57) * mm, "end": v(10725.6, -3401.57) * mm});
            skLineSegment(sketch, "E75", {"start": v(0, -6350) * mm, "end": v(6873.54, -6350) * mm});
            skSolve(sketch);
        }
        {
            var Q0;
            Q0=qSketchRegion(id+"F26",true);
            extrude(context, id + "F27", {"entities" : qUnion([Q0]), "operationType" : NewBodyOperationType.REMOVE, "endBound" : BoundingType.THROUGH_ALL, "oppositeDirection" : true, "depth" : 25 * mm});
        }
        {
            var Q0;
            Q0=makeQuery(id+"F17.boolean.opBoolean","MERGE",FACE,{"derivedFrom":[makeQuery(id+"F15.boolean.opBoolean","MERGE",FACE,{"derivedFrom":[makeQuery(id+"F13.boolean.opBoolean","MERGE",FACE,{"derivedFrom":[makeQuery(id+"F3.opExtrude","CAP_FACE",FACE,{"disambiguationData":[OSD([sQuery(id+"F2.wireOp",EDGE,"E4.bottom"),sQuery(id+"F2.wireOp",EDGE,"E4.top"),sQuery(id+"F2.wireOp",EDGE,"E4.left"),sQuery(id+"F2.wireOp",EDGE,"E4.right"),sQuery(id+"F2.wireOp",EDGE,"E5.top"),sQuery(id+"F2.wireOp",EDGE,"E6.top"),sQuery(id+"F2.wireOp",EDGE,"E6.left"),sQuery(id+"F2.wireOp",EDGE,"E6.right"),sQuery(id+"F2.wireOp",EDGE,"E7.top"),sQuery(id+"F2.wireOp",EDGE,"E7.left"),sQuery(id+"F2.wireOp",EDGE,"E7.right"),sQuery(id+"F2.wireOp",EDGE,"E8.top"),sQuery(id+"F2.wireOp",EDGE,"E8.left"),sQuery(id+"F2.wireOp",EDGE,"E8.right"),sQuery(id+"F2.wireOp",EDGE,"E9.top"),sQuery(id+"F2.wireOp",EDGE,"E9.left"),sQuery(id+"F2.wireOp",EDGE,"E10.top"),sQuery(id+"F2.wireOp",EDGE,"E10.right"),sQuery(id+"F2.wireOp",EDGE,"E11.top"),sQuery(id+"F2.wireOp",EDGE,"E11.left"),sQuery(id+"F2.wireOp",EDGE,"E11.right"),sQuery(id+"F2.wireOp",EDGE,"E12.bottom"),sQuery(id+"F2.wireOp",EDGE,"E12.top"),sQuery(id+"F2.wireOp",EDGE,"E12.left"),sQuery(id+"F2.wireOp",EDGE,"E12.right"),sQuery(id+"F2.wireOp",EDGE,"E13.trimOffspring"),sQuery(id+"F2.wireOp",EDGE,"E14.trimOffspring"),sQuery(id+"F2.wireOp",EDGE,"E15.top"),sQuery(id+"F2.wireOp",EDGE,"E15.right"),sQuery(id+"F2.wireOp",EDGE,"E16.top"),sQuery(id+"F2.wireOp",EDGE,"E17.trimOffspring"),sQuery(id+"F2.wireOp",EDGE,"E18.trimOffspring"),sQuery(id+"F2.wireOp",EDGE,"E19"),sQuery(id+"F2.wireOp",EDGE,"E20"),sQuery(id+"F2.wireOp",EDGE,"E21")])],"isStart":false}),makeQuery(id+"F13.opExtrude","CAP_FACE",FACE,{"disambiguationData":[OSD([sQuery(id+"F12.wireOp",EDGE,"E31.bottom"),sQuery(id+"F12.wireOp",EDGE,"E31.top"),sQuery(id+"F12.wireOp",EDGE,"E31.left"),sQuery(id+"F12.wireOp",EDGE,"E31.right")])],"isStart":true})]}),makeQuery(id+"F15.opExtrude","SWEPT_FACE",FACE,{"disambiguationData":[OSD([sQuery(id+"F14.wireOp",EDGE,"E47")])]})]}),makeQuery(id+"F17.opExtrude","SWEPT_FACE",FACE,{"disambiguationData":[OSD([sQuery(id+"F16.wireOp",EDGE,"E58")])]})]});
            var sketch = newSketch(context, id + "F28", { "sketchPlane" : qUnion([Q0])});
            skLineSegment(sketch, "E76.bottom", {"start": v(9400, -6350) * mm, "end": v(7290, -6350) * mm});
            skLineSegment(sketch, "E76.top", {"start": v(9400, -3610) * mm, "end": v(7290, -3610) * mm});
            skLineSegment(sketch, "E76.left", {"start": v(9400, -6350) * mm, "end": v(9400, -3610) * mm});
            skLineSegment(sketch, "E76.right", {"start": v(7290, -6350) * mm, "end": v(7290, -3610) * mm});
            skLineSegment(sketch, "E77.bottom", {"start": v(7440, -3760) * mm, "end": v(9240, -3760) * mm});
            skLineSegment(sketch, "E77.top", {"start": v(7440, -6150) * mm, "end": v(9240, -6150) * mm});
            skLineSegment(sketch, "E77.left", {"start": v(7440, -3760) * mm, "end": v(7440, -6150) * mm});
            skLineSegment(sketch, "E77.right", {"start": v(9240, -3760) * mm, "end": v(9240, -6150) * mm});
            skSolve(sketch);
        }
        {
            var Q0;
            Q0 = qSketchRegion(id + "F28", true);
            extrude(context, id + "F29", {"entities" : qUnion([Q0]), "operationType" : NewBodyOperationType.ADD, "depth" : 210 * mm, "offsetDistance" : 25 * mm});
        }
        {
            var Q0;
            Q0=makeQuery(id+"F29.boolean.opBoolean","MERGE",FACE,{"derivedFrom":[makeQuery(id+"F3.boolean.opBoolean","MERGE",FACE,{"derivedFrom":[makeQuery(id+"F1.opExtrude","SWEPT_FACE",FACE,{"disambiguationData":[OSD([sQuery(id+"F0.wireOp",EDGE,"E0.top")])]}),makeQuery(id+"F3.opExtrude","SWEPT_FACE",FACE,{"disambiguationData":[OSD([sQuery(id+"F2.wireOp",EDGE,"E12.top")])]})]}),makeQuery(id+"F29.opExtrude","SWEPT_FACE",FACE,{"disambiguationData":[OSD([sQuery(id+"F28.wireOp",EDGE,"E76.bottom")])]})]});
            var sketch = newSketch(context, id + "F30", { "sketchPlane" : qUnion([Q0])});
            skLineSegment(sketch, "E78", {"start": v(9240, 2400) * mm, "end": v(9400, 2400) * mm});
            skLineSegment(sketch, "E79", {"start": v(9400, 2400) * mm, "end": v(9400, 2780) * mm});
            skLineSegment(sketch, "E80", {"start": v(9400, 2780) * mm, "end": v(7440, 2780) * mm});
            skLineSegment(sketch, "E81", {"start": v(7440, 2780) * mm, "end": v(9240, 2400) * mm});
            skSolve(sketch);
        }
        {
            var Q0;
            Q0 = qSketchRegion(id + "F30", true);
            var Q1;
            Q1=makeQuery(id+"F29.boolean.opBoolean","MERGE",FACE,{"derivedFrom":[makeQuery(id+"F3.opExtrude","SWEPT_FACE",FACE,{"disambiguationData":[OSD([sQuery(id+"F2.wireOp",EDGE,"E5.top")])]}),makeQuery(id+"F29.opExtrude","SWEPT_FACE",FACE,{"disambiguationData":[OSD([sQuery(id+"F28.wireOp",EDGE,"E76.top")])]})]});
            extrude(context, id + "F31", {"entities" : qUnion([Q0]), "operationType" : NewBodyOperationType.REMOVE, "endBound" : BoundingType.UP_TO_SURFACE, "oppositeDirection" : true, "depth" : 25 * mm, "endBoundEntityFace" : qUnion([Q1]), "offsetDistance" : 25 * mm});
        }
        {
            var Q0;
            Q0=makeQuery(id+"F29.opExtrude","CAP_FACE",FACE,{"disambiguationData":[OSD([sQuery(id+"F28.wireOp",EDGE,"E76.bottom"),sQuery(id+"F28.wireOp",EDGE,"E76.top"),sQuery(id+"F28.wireOp",EDGE,"E76.left"),sQuery(id+"F28.wireOp",EDGE,"E76.right"),sQuery(id+"F28.wireOp",EDGE,"E77.bottom"),sQuery(id+"F28.wireOp",EDGE,"E77.top"),sQuery(id+"F28.wireOp",EDGE,"E77.left"),sQuery(id+"F28.wireOp",EDGE,"E77.right")])],"isStart":false});
            var sketch = newSketch(context, id + "F32", { "sketchPlane" : qUnion([Q0])});
            skLineSegment(sketch, "E82.bottom", {"start": v(7290, -3760) * mm, "end": v(9400, -3760) * mm});
            skLineSegment(sketch, "E82.top", {"start": v(7290, -6350) * mm, "end": v(9400, -6350) * mm});
            skLineSegment(sketch, "E82.left", {"start": v(7290, -6350) * mm, "end": v(7290, -3760) * mm});
            skLineSegment(sketch, "E82.right", {"start": v(9400, -6350) * mm, "end": v(9400, -3760) * mm});
            skLineSegment(sketch, "E83.bottom", {"start": v(6751.48, -3293.95) * mm, "end": v(10726.38, -3293.95) * mm});
            skLineSegment(sketch, "E83.top", {"start": v(6751.48, -6450.85) * mm, "end": v(10726.38, -6450.85) * mm});
            skLineSegment(sketch, "E83.left", {"start": v(6751.48, -3293.95) * mm, "end": v(6751.48, -6450.85) * mm});
            skLineSegment(sketch, "E83.right", {"start": v(10726.38, -3293.95) * mm, "end": v(10726.38, -6450.85) * mm});
            skSolve(sketch);
        }
        {
            var Q0;
            Q0 = qSketchRegion(id + "F32", true);
            extrude(context, id + "F33", {"entities" : qUnion([Q0]), "operationType" : NewBodyOperationType.REMOVE, "endBound" : BoundingType.THROUGH_ALL, "oppositeDirection" : true, "depth" : 25 * mm, "offsetDistance" : 25 * mm});
        }
        {
            var Q0;
            Q0=makeQuery(id+"F29.boolean.opBoolean","MERGE",FACE,{"derivedFrom":[makeQuery(id+"F3.opExtrude","SWEPT_FACE",FACE,{"disambiguationData":[OSD([sQuery(id+"F2.wireOp",EDGE,"E10.right")])]}),makeQuery(id+"F29.opExtrude","SWEPT_FACE",FACE,{"disambiguationData":[OSD([sQuery(id+"F28.wireOp",EDGE,"E77.left")])]})]});
            var sketch = newSketch(context, id + "F34", { "sketchPlane" : qUnion([Q0])});
            skCircle(sketch, "E84", {"center": v(-5510, 1750) * mm, "radius": 6 * mm});
            skSolve(sketch);
        }
        {
            var Q0;
            Q0 = qSketchRegion(id + "F34", true);
            extrude(context, id + "F35", {"entities" : qUnion([Q0]), "operationType" : NewBodyOperationType.REMOVE, "oppositeDirection" : true, "depth" : 300 * mm, "offsetDistance" : 25 * mm});
        }
    });
